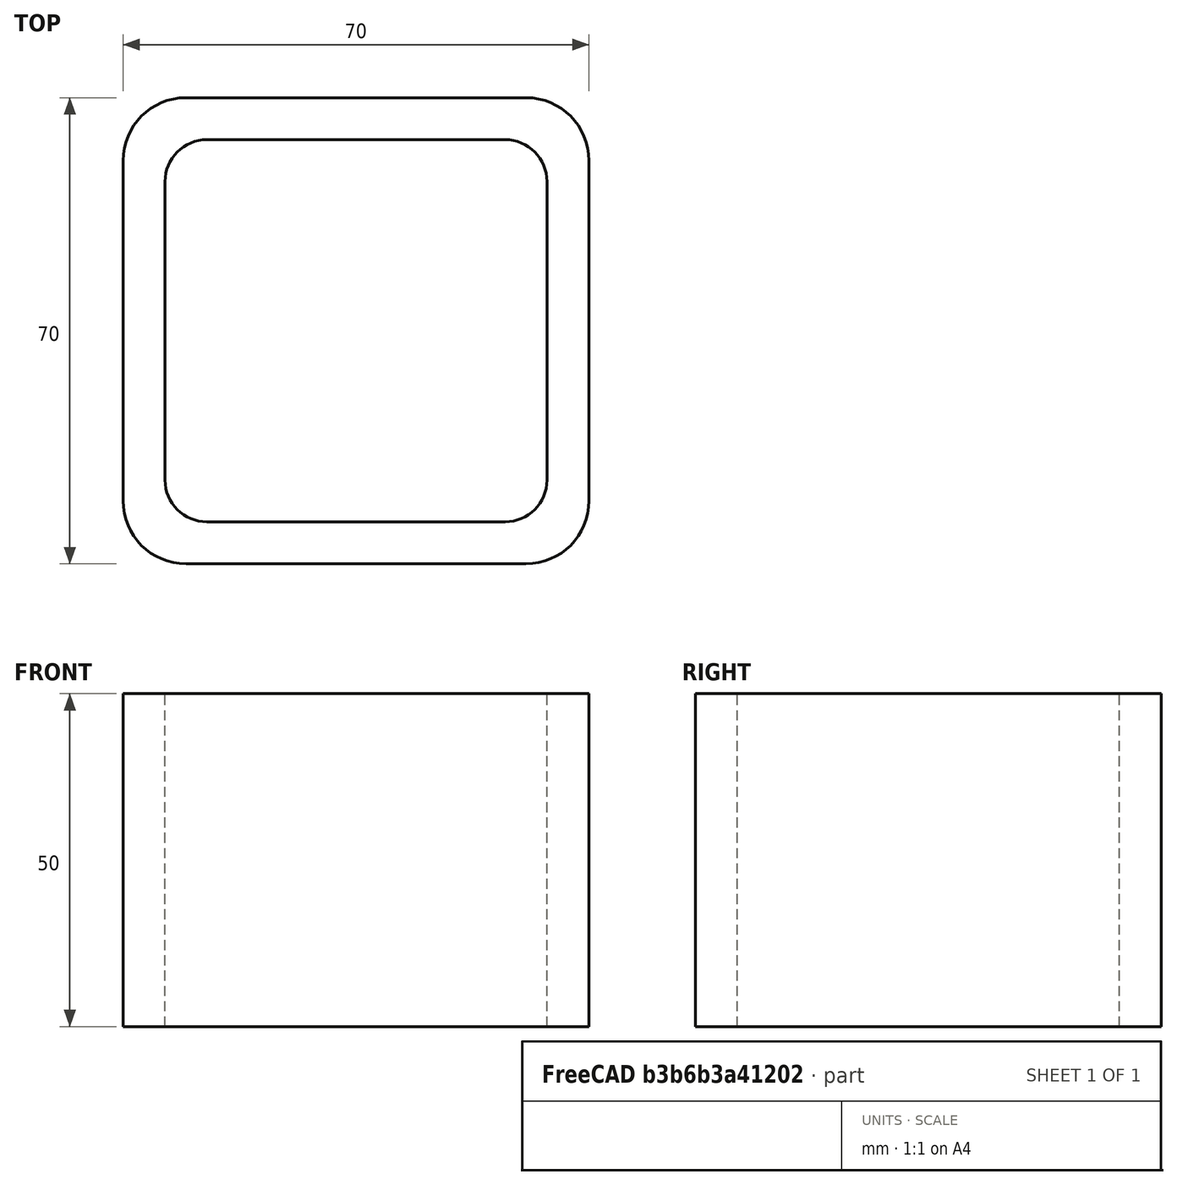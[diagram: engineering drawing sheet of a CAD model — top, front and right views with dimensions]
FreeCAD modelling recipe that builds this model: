
FCSTD DOCUMENT  (FreeCAD 0.15R4671 (Git))
Label: Square hollow section 70x70x6.3 EN10219 S235JRH
License: All rights reserved
LicenseURL: http://en.wikipedia.org/wiki/All_rights_reserved
objects: Sketcher::SketchObject×1, Part::Extrusion×1
note: 2 computed .brp shape members not serialized (recipe doc carries the construction recipe); baked Part::Feature solids carry a one-line shape summary decoded from their .brp

FEATURE [Sketcher::SketchObject] Sketch
  sketch-geometry (16):
    g0: LineSegment StartX=-22.4 StartY=28.7 StartZ=0 EndX=22.4 EndY=28.7 EndZ=0
    g1: LineSegment StartX=28.7 StartY=22.4 StartZ=0 EndX=28.7 EndY=-22.4 EndZ=0
    g2: LineSegment StartX=22.4 StartY=-28.7 StartZ=0 EndX=-22.4 EndY=-28.7 EndZ=0
    g3: LineSegment StartX=-28.7 StartY=-22.4 StartZ=0 EndX=-28.7 EndY=22.4 EndZ=0
    g4: LineSegment StartX=-25.55 StartY=35 StartZ=0 EndX=25.55 EndY=35 EndZ=0
    g5: LineSegment StartX=35 StartY=25.55 StartZ=0 EndX=35 EndY=-25.55 EndZ=0
    g6: LineSegment StartX=25.55 StartY=-35 StartZ=0 EndX=-25.55 EndY=-35 EndZ=0
    g7: LineSegment StartX=-35 StartY=-25.55 StartZ=0 EndX=-35 EndY=25.55 EndZ=0
    g8: ArcOfCircle CenterX=-22.4 CenterY=22.4 CenterZ=0 NormalX=0 NormalY=0 NormalZ=1 Radius=6.3 StartAngle=1.5708 EndAngle=3.14159
    g9: ArcOfCircle CenterX=22.4 CenterY=22.4 CenterZ=0 NormalX=0 NormalY=0 NormalZ=1 Radius=6.3 StartAngle=0 EndAngle=1.5708
    g10: ArcOfCircle CenterX=22.4 CenterY=-22.4 CenterZ=0 NormalX=0 NormalY=0 NormalZ=1 Radius=6.3 StartAngle=4.71239 EndAngle=6.28319
    g11: ArcOfCircle CenterX=-22.4 CenterY=-22.4 CenterZ=0 NormalX=0 NormalY=0 NormalZ=1 Radius=6.3 StartAngle=3.14159 EndAngle=4.71239
    g12: ArcOfCircle CenterX=25.55 CenterY=25.55 CenterZ=0 NormalX=0 NormalY=0 NormalZ=1 Radius=9.45 StartAngle=0 EndAngle=1.5708
    g13: ArcOfCircle CenterX=25.55 CenterY=-25.55 CenterZ=0 NormalX=0 NormalY=0 NormalZ=1 Radius=9.45 StartAngle=4.71239 EndAngle=6.28319
    g14: ArcOfCircle CenterX=-25.55 CenterY=-25.55 CenterZ=0 NormalX=0 NormalY=0 NormalZ=1 Radius=9.45 StartAngle=3.14159 EndAngle=4.71239
    g15: ArcOfCircle CenterX=-25.55 CenterY=25.55 CenterZ=0 NormalX=0 NormalY=0 NormalZ=1 Radius=9.45 StartAngle=1.5708 EndAngle=3.14159
  constraints (36):
    c: Horizontal(g2)
    c: Vertical(g3)
    c: Horizontal(g6)
    c: Vertical(g7)
    c: Tangent(g3,g8) = 1.5708
    c: Tangent(g0,g8) = 1.5708
    c: Tangent(g0,g9) = 1.5708
    c: Tangent(g1,g9) = 1.5708
    c: Tangent(g1,g10) = 1.5708
    c: Tangent(g2,g10) = 1.5708
    c: Tangent(g2,g11) = 1.5708
    c: Tangent(g3,g11) = 1.5708
    c: Tangent(g4,g12) = 1.5708
    c: Tangent(g5,g12) = 1.5708
    c: Tangent(g5,g13) = 1.5708
    c: Tangent(g6,g13) = 1.5708
    c: Tangent(g6,g14) = 1.5708
    c: Tangent(g7,g14) = 1.5708
    c: Tangent(g7,g15) = 1.5708
    c: Tangent(g4,g15) = 1.5708
    c: Equal(g9,g8)
    c: Equal(g9,g11)
    c: Equal(g9,g10)
    c: Equal(g12,g15)
    c: Equal(g12,g14)
    c: Equal(g12,g13)
    c: Symmetric(g4,g6,g-1)
    c: Symmetric(g7,g5,g-2)
    c: DistanceY(g4,g6) = -70
    c: DistanceX(g7,g5) = 70
    c: Symmetric(g3,g1,g-2)
    c: Symmetric(g0,g2,g-1)
    c: DistanceY(g0,g4) = 6.3
    c: DistanceX(g5,g1) = -6.3
    c: Radius(g9) = 6.3
    c: Radius(g12) = 9.45
FEATURE [Part::Extrusion] Extrude  label="Square hollow section 70x70x6.3 EN10219 S235JRH"
  Base = -> Sketch
  Dir = (0,0,50)
  Solid = true
